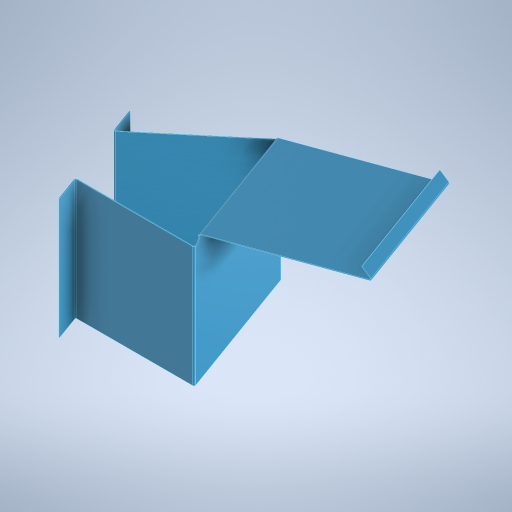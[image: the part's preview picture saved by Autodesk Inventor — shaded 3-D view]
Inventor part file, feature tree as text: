
AUTODESK INVENTOR PART (.ipt)
format: ipt  version: 2024 (Build 280153000, 153)  size: 407,552 bytes
history: native  units: mm
features: sheet_metal_op x7, other x2, sketch x1, plane x1
ambient origin geometry x8: Origin, YZ Plane, XZ Plane, XY Plane, X Axis, Y Axis, Z Axis, Center Point
bodies: Solid1 (feature_tree)
feature tree (11):
  sheet_metal_op  "Face1"
  sketch  "Sketch3"  dims[d0=1800.0mm d1=500.0mm d2=3.048mm d3=300.0mm d4=490.0mm d5=3.048mm d6=1.524mm d7=6.096mm d8=3.048mm d9=19.198622mm d10=3.048mm d11=3.048mm d12=1.524mm d13=6.096mm d14=3.048mm d15=19.198622mm d16=3.048mm d17=110.0mm d18=490.0mm d19=90.0deg d20=3.048mm d21=1.524mm d22=6.096mm d23=3.048mm d24=19.198622mm d25=3.048mm d26=3.048mm d27=1.524mm d28=6.096mm d29=3.048mm d30=19.198622mm d31=3.048mm d32=270.0mm d33=540.0mm d34=632.0mm d49=20.0mm d50=20.0mm d51=5.0mm d52=3.048mm d53=1.524mm d54=6.096mm d55=3.048mm d56=90.0deg d57=3.048mm d58=50.0mm d59=3.048mm d60=1.524mm d61=6.096mm d62=3.048mm d63=22.68928mm d64=3.048mm]
  sheet_metal_op  "Fold1"
  sheet_metal_op  "Fold2"
  sheet_metal_op  "Fold3"
  sheet_metal_op  "Fold4"
  plane  "Work Plane1"
  sheet_metal_op  "Fold7"
  sheet_metal_op  "Fold8"
  other  "Plate1"
  other  "Definition1"
